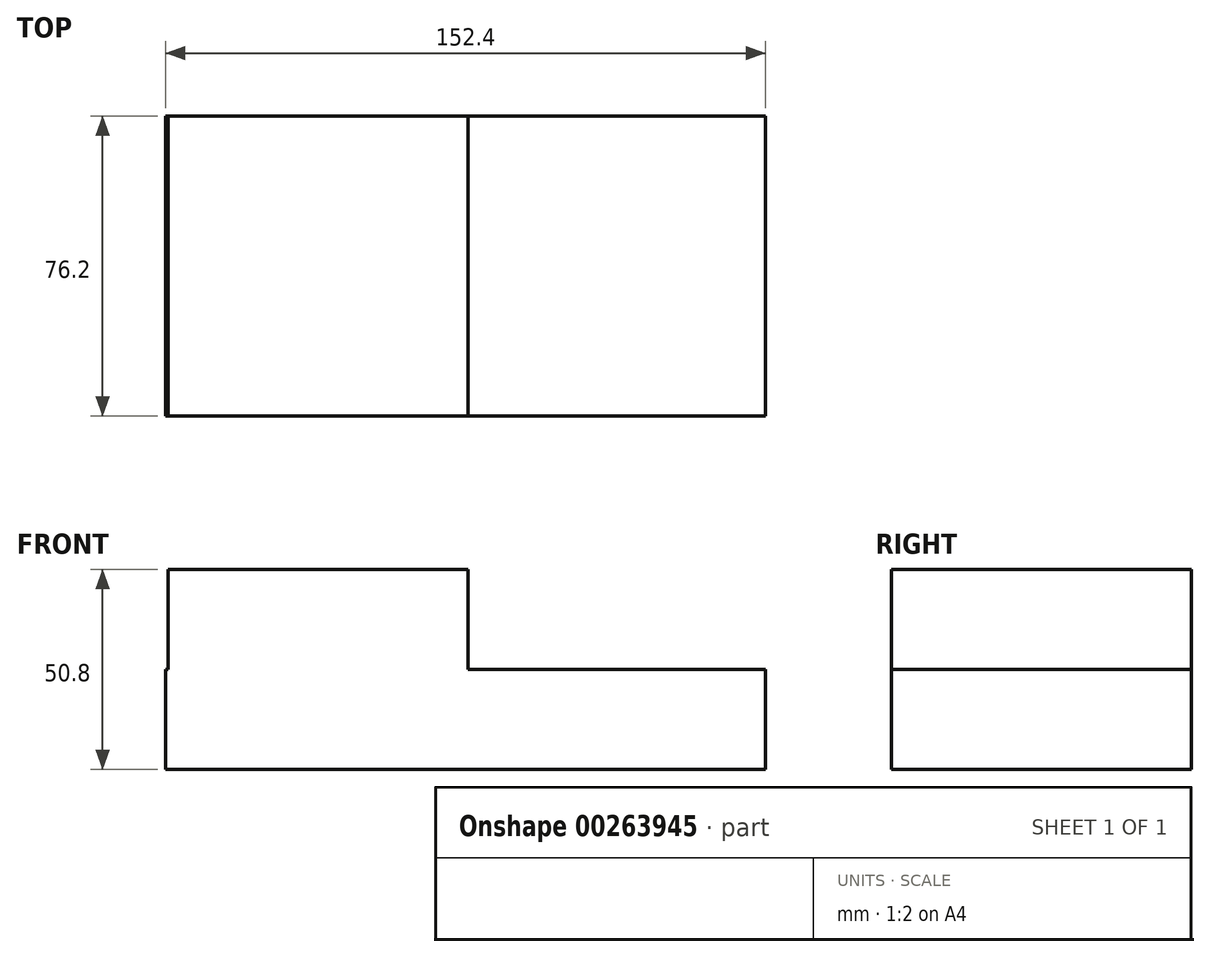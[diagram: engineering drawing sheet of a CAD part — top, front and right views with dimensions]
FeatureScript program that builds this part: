
annotation { "Feature Type Name" : "Feature", "Feature Type Description" : "" }
export const myFeature = defineFeature(function(context is Context, id is Id, definition is map)
    precondition{}
    {
        {
            var Q0;
            Q0=qCreatedBy(makeId("Front.planeOp"),FACE);
            var sketch = newSketch(context, id + "F0", { "sketchPlane" : qUnion([Q0])});
            skLineSegment(sketch, "E0.bottom", {"start": v(0, 0) * mm, "end": v(-76.2, 0) * mm});
            skLineSegment(sketch, "E0.top", {"start": v(0, 25.4) * mm, "end": v(-76.2, 25.4) * mm});
            skLineSegment(sketch, "E0.left", {"start": v(0, 0) * mm, "end": v(0, 25.4) * mm});
            skLineSegment(sketch, "E0.right", {"start": v(-76.2, 0) * mm, "end": v(-76.2, 25.4) * mm});
            skSolve(sketch);
        }
        {
            var Q0;
            Q0=qCreatedBy(makeId("Front.planeOp"),FACE);
            var sketch = newSketch(context, id + "F1", { "sketchPlane" : qUnion([Q0])});
            skLineSegment(sketch, "E1.bottom", {"start": v(-76.88, 0) * mm, "end": v(75.52, 0) * mm});
            skLineSegment(sketch, "E1.top", {"start": v(-76.88, -25.4) * mm, "end": v(75.52, -25.4) * mm});
            skLineSegment(sketch, "E1.left", {"start": v(-76.88, 0) * mm, "end": v(-76.88, -25.4) * mm});
            skLineSegment(sketch, "E1.right", {"start": v(75.52, 0) * mm, "end": v(75.52, -25.4) * mm});
            skSolve(sketch);
        }
        {
            var Q0;
            Q0 = qSketchRegion(id + "F1", true);
            extrude(context, id + "F2", {"entities" : qUnion([Q0]), "depth" : 76.2 * mm});
        }
        {
            var Q0;
            Q0=makeQuery(id+"F0.imprint","IMPRINT",FACE,{"disambiguationData":[TD([[makeQuery(id+"F0.imprint","IMPRINT",EDGE,{"derivedFrom":sQuery(id+"F0.wireOp",EDGE,"E0.bottom")}),-1.0]])]});
            extrude(context, id + "F3", {"entities" : qUnion([Q0]), "operationType" : NewBodyOperationType.ADD, "depth" : 76.2 * mm});
        }
    });
